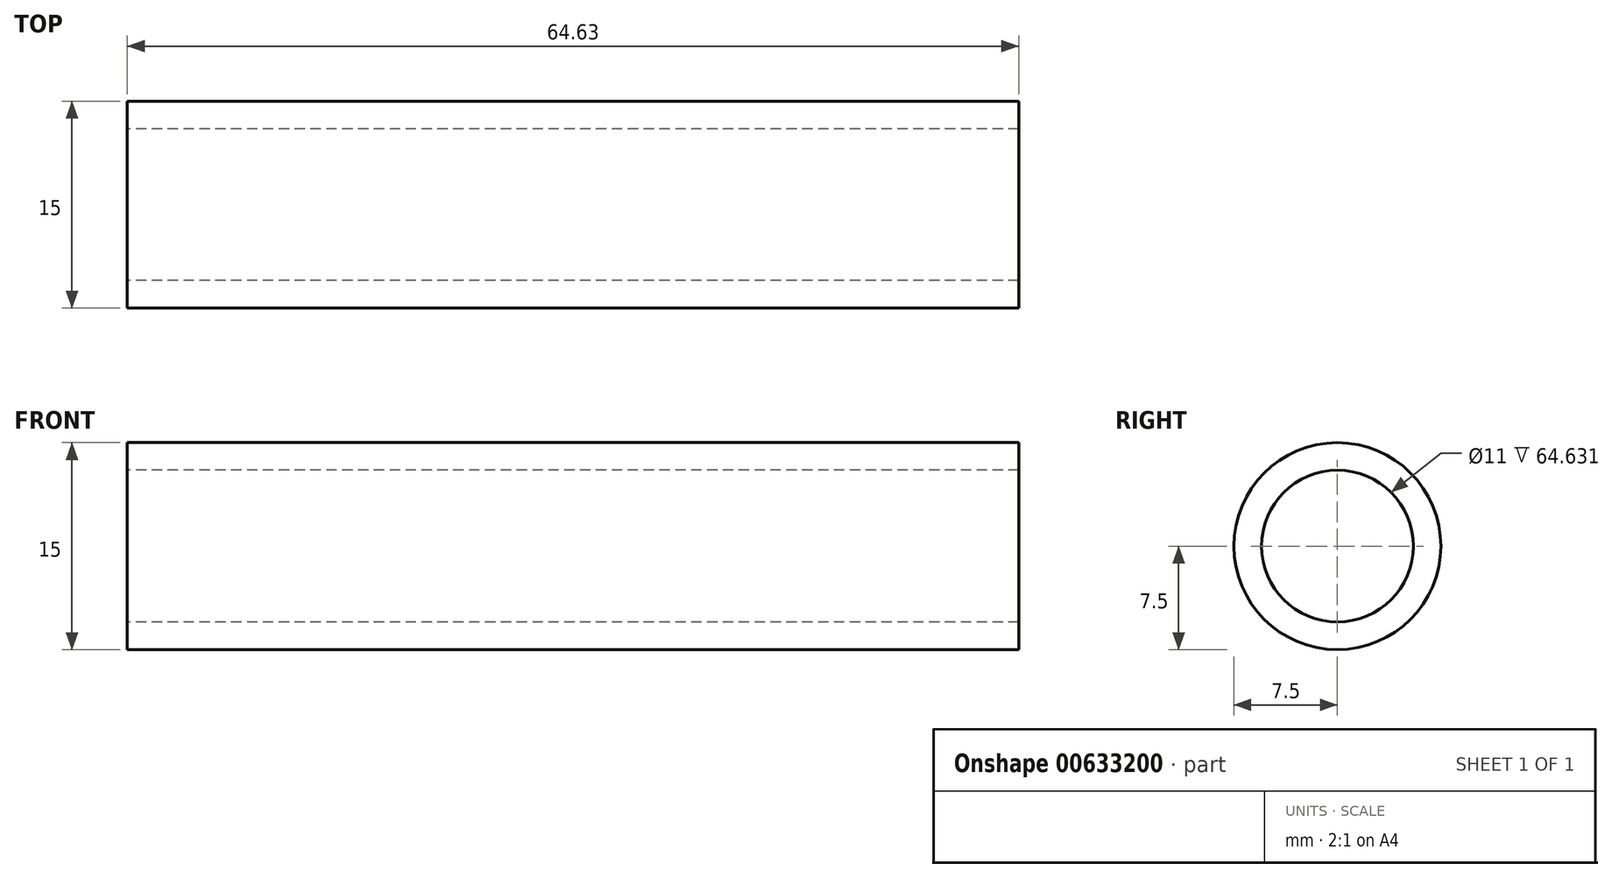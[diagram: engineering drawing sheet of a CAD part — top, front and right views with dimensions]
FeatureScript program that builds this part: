
annotation { "Feature Type Name" : "Feature", "Feature Type Description" : "" }
export const myFeature = defineFeature(function(context is Context, id is Id, definition is map)
    precondition{}
    {
        {
            var Q0;
            Q0=qCreatedBy(makeId("Front.planeOp"),FACE);
            var sketch = newSketch(context, id + "F0", { "sketchPlane" : qUnion([Q0])});
            skLineSegment(sketch, "E0", {"start": v(-63.31, 0) * mm, "end": v(74.38, 0) * mm, "construction": true});
            skLineSegment(sketch, "E1", {"start": v(-32, 7.5) * mm, "end": v(32.63, 7.5) * mm});
            skLineSegment(sketch, "E2", {"start": v(-32, 7.5) * mm, "end": v(-32, 5.5) * mm});
            skLineSegment(sketch, "E3", {"start": v(-32, 5.5) * mm, "end": v(32.63, 5.5) * mm});
            skLineSegment(sketch, "E4", {"start": v(32.63, 5.5) * mm, "end": v(32.63, 7.5) * mm});
            skSolve(sketch);
        }
        {
            var Q0;
            Q0=qSketchRegion(id+"F0",true);
            var Q1;
            Q1=sQuery(id+"F0.wireOp",EDGE,"E0");
            revolve(context, id + "F1", {"entities" : qUnion([Q0]), "axis" : qUnion([Q1]), "revolveType" : RevolveType.FULL});
        }
    });
